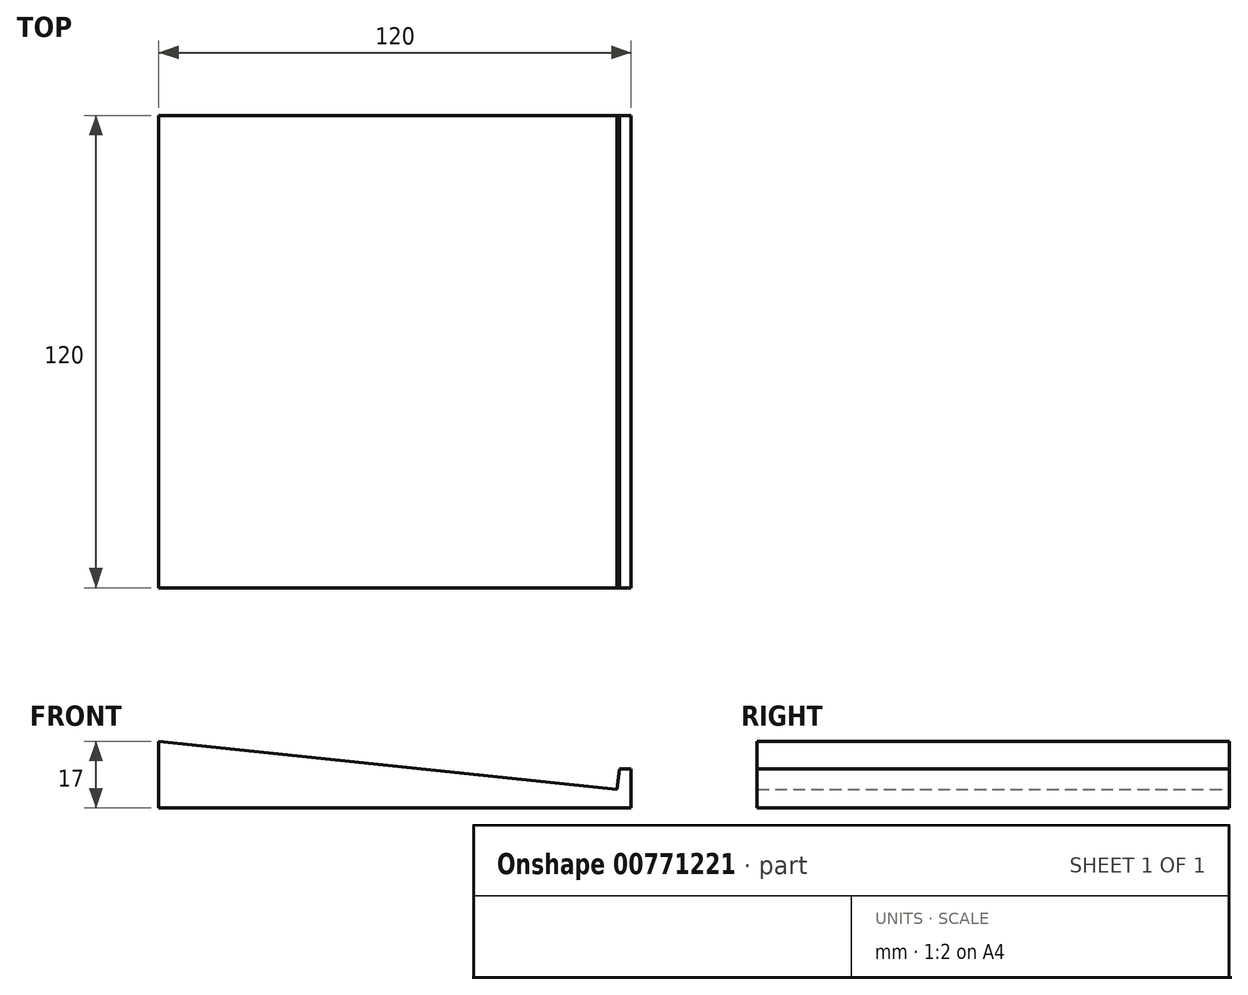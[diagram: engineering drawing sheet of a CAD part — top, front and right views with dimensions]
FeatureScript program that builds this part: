
annotation { "Feature Type Name" : "Feature", "Feature Type Description" : "" }
export const myFeature = defineFeature(function(context is Context, id is Id, definition is map)
    precondition{}
    {
        {
            var Q0;
            Q0=qCreatedBy(makeId("Front.planeOp"),FACE);
            var sketch = newSketch(context, id + "F0", { "sketchPlane" : qUnion([Q0])});
            skLineSegment(sketch, "E0", {"start": v(120, 0) * mm, "end": v(0, 0) * mm});
            skLineSegment(sketch, "E1", {"start": v(0, 0) * mm, "end": v(0, 17) * mm});
            skLineSegment(sketch, "E2", {"start": v(0, 17) * mm, "end": v(116.45, 4.76) * mm});
            skLineSegment(sketch, "E3", {"start": v(116.45, 4.76) * mm, "end": v(117, 10) * mm});
            skLineSegment(sketch, "E4", {"start": v(117, 10) * mm, "end": v(120, 10) * mm});
            skLineSegment(sketch, "E5", {"start": v(120, 10) * mm, "end": v(120, 0) * mm});
            skSolve(sketch);
        }
        {
            var Q0;
            Q0 = qSketchRegion(id + "F0", true);
            extrude(context, id + "F1", {"entities" : qUnion([Q0]), "depth" : 120 * mm, "offsetDistance" : 25 * mm});
        }
    });
